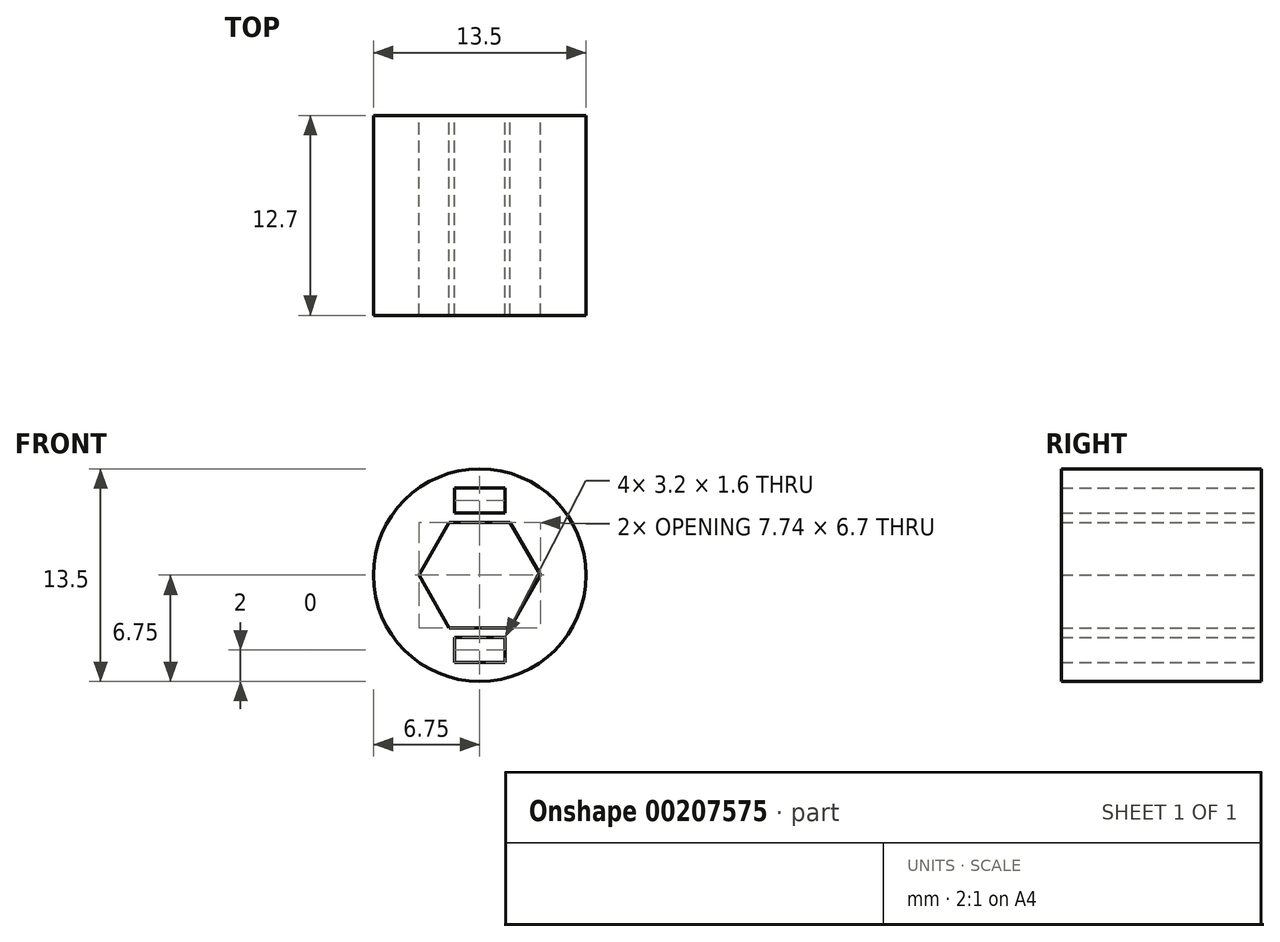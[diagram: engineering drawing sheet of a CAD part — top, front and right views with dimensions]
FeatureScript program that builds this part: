
annotation { "Feature Type Name" : "Feature", "Feature Type Description" : "" }
export const myFeature = defineFeature(function(context is Context, id is Id, definition is map)
    precondition{}
    {
        {
            var Q0;
            Q0=qCreatedBy(makeId("Front.planeOp"),FACE);
            var sketch = newSketch(context, id + "F0", { "sketchPlane" : qUnion([Q0])});
            skCircle(sketch, "E0.cCircle", {"center": v(0, 0) * mm, "radius": 3.35 * mm, "construction": true});
            skLineSegment(sketch, "E0.0", {"start": v(3.87, 0) * mm, "end": v(1.93, -3.35) * mm});
            skLineSegment(sketch, "E0.1", {"start": v(1.93, -3.35) * mm, "end": v(-1.93, -3.35) * mm});
            skLineSegment(sketch, "E0.2", {"start": v(-1.93, -3.35) * mm, "end": v(-3.87, 0) * mm});
            skLineSegment(sketch, "E0.3", {"start": v(-3.87, 0) * mm, "end": v(-1.93, 3.35) * mm});
            skLineSegment(sketch, "E0.4", {"start": v(-1.93, 3.35) * mm, "end": v(1.93, 3.35) * mm});
            skLineSegment(sketch, "E0.5", {"start": v(1.93, 3.35) * mm, "end": v(3.87, 0) * mm});
            skLineSegment(sketch, "E1", {"start": v(0, 3.35) * mm, "end": v(0, -3.35) * mm, "construction": true});
            skCircle(sketch, "E2", {"center": v(0, 0) * mm, "radius": 6.75 * mm});
            skLineSegment(sketch, "E3", {"start": v(0, 3.35) * mm, "end": v(-1.93, 3.35) * mm});
            skLineSegment(sketch, "E4", {"start": v(1.93, 3.35) * mm, "end": v(0, 3.35) * mm});
            skLineSegment(sketch, "E5", {"start": v(1.93, -3.35) * mm, "end": v(3.87, 0) * mm});
            skLineSegment(sketch, "E6", {"start": v(0, 3.35) * mm, "end": v(0, 3.35) * mm});
            skLineSegment(sketch, "E7", {"start": v(-1.6, -5.55) * mm, "end": v(1.6, -5.55) * mm});
            skLineSegment(sketch, "E8", {"start": v(-1.6, 5.55) * mm, "end": v(1.6, 5.55) * mm});
            skLineSegment(sketch, "E9", {"start": v(-1.6, 5.55) * mm, "end": v(-1.6, 3.95) * mm});
            skLineSegment(sketch, "E10", {"start": v(-1.6, 3.95) * mm, "end": v(1.6, 3.95) * mm});
            skLineSegment(sketch, "E11", {"start": v(1.6, 3.95) * mm, "end": v(1.6, 5.55) * mm});
            skLineSegment(sketch, "E12", {"start": v(-1.6, -5.55) * mm, "end": v(-1.6, -3.95) * mm});
            skLineSegment(sketch, "E13", {"start": v(-1.6, -3.95) * mm, "end": v(1.6, -3.95) * mm});
            skLineSegment(sketch, "E14", {"start": v(1.6, -3.95) * mm, "end": v(1.6, -5.55) * mm});
            skLineSegment(sketch, "E15", {"start": v(0, -3.35) * mm, "end": v(0, -3.95) * mm, "construction": true});
            skLineSegment(sketch, "E16", {"start": v(0, 3.35) * mm, "end": v(0, 3.95) * mm, "construction": true});
            skSolve(sketch);
        }
        {
            var Q0;
            Q0=makeQuery(id+"F0.imprint","IMPRINT",FACE,{"disambiguationData":[TD([[makeQuery(id+"F0.imprint","IMPRINT",EDGE,{"derivedFrom":sQuery(id+"F0.wireOp",EDGE,"E0.3")}),1.0]])]});
            extrude(context, id + "F1", {"entities" : qUnion([Q0]), "depth" : 12.7 * mm});
        }
        {
            var Q0;
            Q0=makeQuery(id+"F1.opExtrude","SWEPT_BODY",BODY,{"disambiguationData":[OSD([sQuery(id+"F0.wireOp",EDGE,"E0.0"),sQuery(id+"F0.wireOp",EDGE,"E0.1"),sQuery(id+"F0.wireOp",EDGE,"E0.2"),sQuery(id+"F0.wireOp",EDGE,"E0.3"),sQuery(id+"F0.wireOp",EDGE,"E0.4"),sQuery(id+"F0.wireOp",EDGE,"E0.5"),sQuery(id+"F0.wireOp",EDGE,"E2")])]});
            transform(context, id + "F2", {"entities" : qUnion([Q0]), "transformType" : TransformType.TRANSLATION_3D, "dx" : 0 * mm, "dy" : 0 * mm, "dz" : 0 * mm, "makeCopy" : true});
        }
        {
            var Q0;
            Q0=qCreatedBy(makeId("Top.planeOp"),FACE);
            cPlane(context, id + "F3", {"entities" : qUnion([Q0]), "cplaneType" : CPlaneType.OFFSET, "offset" : 7.11 * mm, "oppositeDirection" : true, "width" : 152.4 * mm, "height" : 152.4 * mm});
        }
    });
